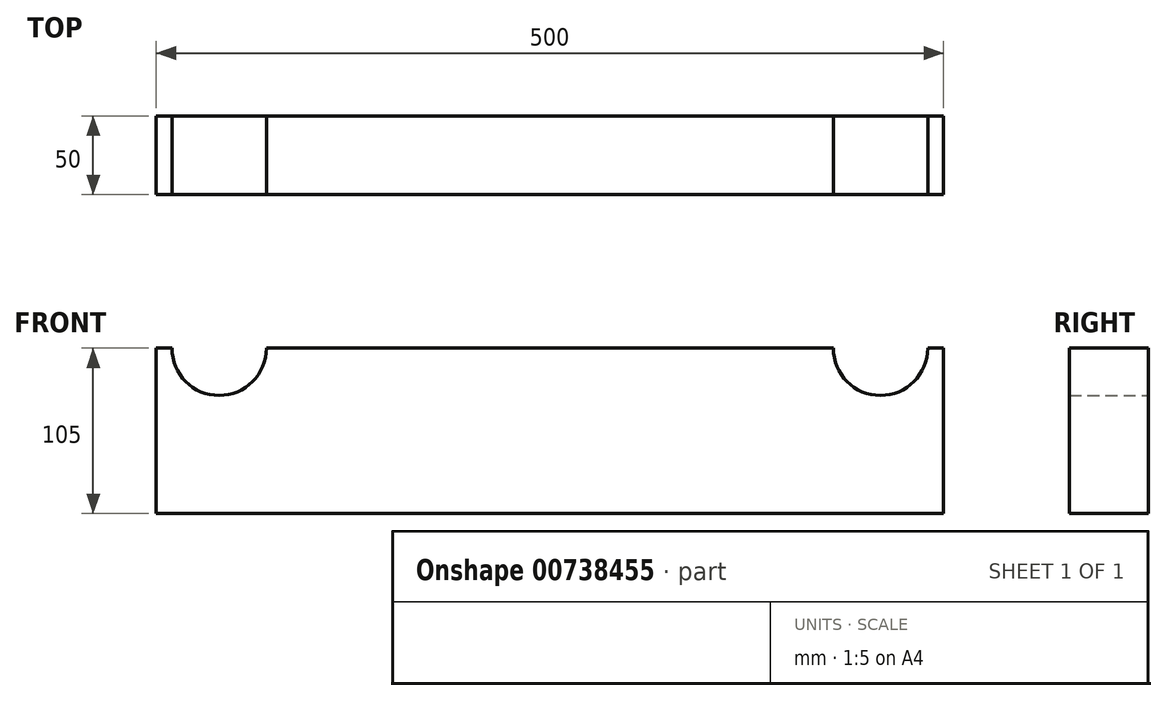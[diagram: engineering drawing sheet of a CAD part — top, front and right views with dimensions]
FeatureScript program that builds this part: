
annotation { "Feature Type Name" : "Feature", "Feature Type Description" : "" }
export const myFeature = defineFeature(function(context is Context, id is Id, definition is map)
    precondition{}
    {
        {
            var Q0;
            Q0=qCreatedBy(makeId("Front.planeOp"),FACE);
            var sketch = newSketch(context, id + "F0", { "sketchPlane" : qUnion([Q0])});
            skLineSegment(sketch, "E0.bottom", {"start": v(-250, 52.5) * mm, "end": v(-240, 52.5) * mm});
            skLineSegment(sketch, "E0.top", {"start": v(-250, -52.5) * mm, "end": v(250, -52.5) * mm});
            skLineSegment(sketch, "E0.left", {"start": v(-250, 52.5) * mm, "end": v(-250, -52.5) * mm});
            skLineSegment(sketch, "E0.right", {"start": v(250, 52.5) * mm, "end": v(250, -52.5) * mm});
            skPoint(sketch, "E0.middle", {"position": v(0, 0) * mm});
            skArc(sketch, "E1", {"start": v(-240, 52.5) * mm, "mid": v(-210, 22.5) * mm, "end": v(-180, 52.5) * mm});
            skArc(sketch, "E2.MirrorC", {"start": v(240, 52.5) * mm, "mid": v(210, 22.5) * mm, "end": v(180, 52.5) * mm});
            skLineSegment(sketch, "E3.trimOffspring", {"start": v(-180, 52.5) * mm, "end": v(180, 52.5) * mm});
            skLineSegment(sketch, "E4.trimOffspring", {"start": v(240, 52.5) * mm, "end": v(250, 52.5) * mm});
            skSolve(sketch);
        }
        {
            var Q0;
            Q0=makeQuery(id+"F0.imprint","IMPRINT",FACE,{"disambiguationData":[TD([[makeQuery(id+"F0.imprint","IMPRINT",EDGE,{"derivedFrom":sQuery(id+"F0.wireOp",EDGE,"E0.bottom")}),-1.0]])]});
            extrude(context, id + "F1", {"entities" : qUnion([Q0]), "depth" : 50 * mm, "offsetDistance" : 25 * mm});
        }
    });
